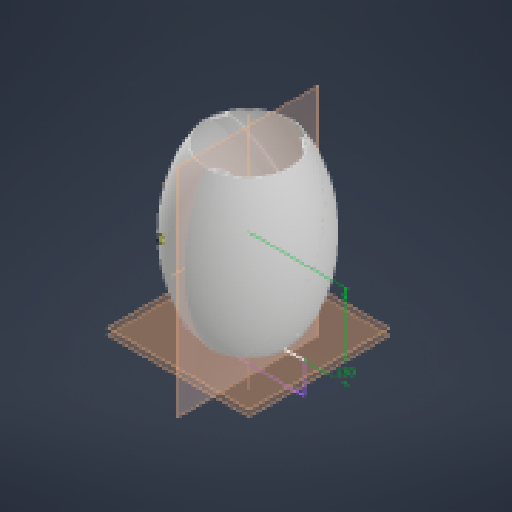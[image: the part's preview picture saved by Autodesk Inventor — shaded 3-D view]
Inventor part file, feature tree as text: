
AUTODESK INVENTOR PART (.ipt)
format: ipt  version: 2023 (Build 270158000, 158)  size: 2,408,960 bytes
history: native  units: mm
features: sketch x13, extrude x8, projected_geometry x6, plane x5, other x5, pattern_circular x4, revolve x2, sweep x1, chamfer x1, shell x1, reference x1
ambient origin geometry x8: Origin, YZ Plane, XZ Plane, XY Plane, X Axis, Y Axis, Z Axis, Center Point
bodies: Solid1 (feature_tree)
feature tree (47):
  revolve  "Revolution1"  [1 undecoded]
  sketch  "3D Sketch1"
  plane  "Work Plane1"
  sweep  "Sweep1"
  pattern_circular  "Circular Pattern1"  Count=3 Angle=360.0deg
  extrude  "Extrusion1"  TaperAngle=0.0deg  [1 undecoded]
  plane  "Work Plane3"
  sketch  "Sketch12"  dims[d16=0.2mm]
  plane  "Work Plane6"
  extrude  "Extrusion6"  Depth=1.0mm
  chamfer  "Chamfer2"  Distance=10.0mm
  pattern_circular  "Circular Pattern4"  [2 undecoded]
  shell  "Shell2"  Thickness=4.0mm
  sketch  "Sketch16"  dims[d26=-130.0mm d27=-10.0mm d29=1.0mm d30=10.0mm d31=0.0mm d32=6.0mm d33=4.0mm d34=0.0mm d35=4.0mm d36=4.0mm d37=0.0mm d38=30.0mm d39=360.0deg d51=100.0mm d52=6.0mm d53=4.0mm d54=0.0mm d55=3.5mm d56=1.0mm d57=45.0deg d58=30.0mm d59=360.0deg d61=30.0deg d62=6.0mm d63=4.0mm d64=0.0mm d65=60.0mm d66=360.0deg d68=360.0deg d69=130.0mm d70=0.0mm d71=0.0mm d72=0.0mm d73=0.0mm]
  extrude  "Extrusion8"  Depth=4.0mm
  extrude  "Extrusion2"  Depth=4.0mm TaperAngle=0.0deg
  sketch  "Sketch7"  dims[d13=1.6mm]
  plane  "Work Plane4"
  extrude  "Extrusion3"  Depth=30.0mm TaperAngle=360.0deg
  extrude  "Extrusion4"  Depth=100.0mm
  pattern_circular  "Circular Pattern2"  [2 undecoded]
  extrude  "Extrusion7"  Depth=4.0mm TaperAngle=0.0deg
  pattern_circular  "Circular Pattern5"  Angle=45.0deg  [1 undecoded]
  revolve  "Revolution2"  Angle=360.0deg
  extrude  "Extrusion9"  TaperAngle=30.0deg  [1 undecoded]
  sketch  "Sketch1"  dims[d0=160.0mm d1=100.0mm]
  other  "Helical Curve2"
  other  "Project to Surface1"
  sketch  "Sketch2"  dims[d2=90.0deg d7=1200.0mm d8=637.649mm d9=252.623mm d10=0.0mm]
  sketch  "Sketch3"  dims[d11=15.0mm]
  plane  "Work Plane2"
  sketch  "Sketch6"  dims[d12=3.0mm]
  sketch  "Sketch8"  dims[d14=1.478932mm]
  sketch  "Sketch9"  dims[d15=0.2mm]
  sketch  "Sketch13"  dims[d17=0.2mm]
  sketch  "Sketch14"  dims[d18=0.0mm d19=0.0mm d20=30.0mm d21=360.0deg]
  reference  "Reference1"
  sketch  "Sketch15"  dims[d23=120.0mm d24=0.0mm d25=0.0mm]
  projected_geometry  "Project Cut Edges1"
  projected_geometry  "Project Cut Edges2"
  projected_geometry  "Project Cut Edges3"
  projected_geometry  "Project Cut Edges5"
  projected_geometry  "Project Cut Edges6"
  parser-record x1  (decoder bookkeeping rows leaked as tree rows — omitted from the tree; the rows remain in map.json)
  other  "Assembly1.iam"
  other  "lower_centering_ring:1"
  projected_geometry  "Project Cut Edges7"
note: 8 required parameter values undecoded (feature->parameter linkage not recoverable at this tier; creation-order binding heuristic only, values carry confidence <= 0.55)
note: 1 file-system path scrubbed to <path> (originals preserved in map.json)